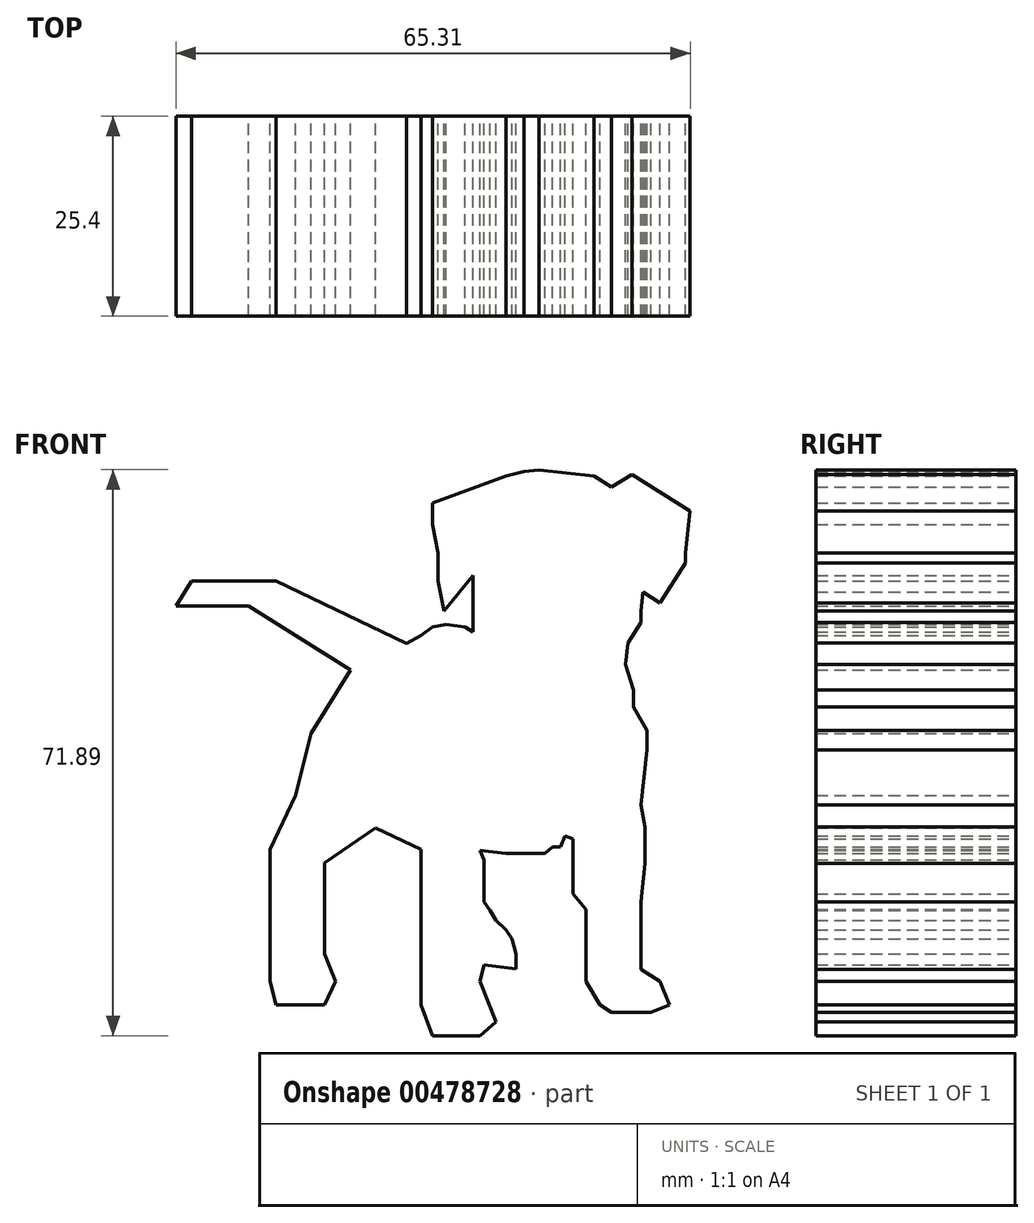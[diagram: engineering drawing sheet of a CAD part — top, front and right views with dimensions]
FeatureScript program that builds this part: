
annotation { "Feature Type Name" : "Feature", "Feature Type Description" : "" }
export const myFeature = defineFeature(function(context is Context, id is Id, definition is map)
    precondition{}
    {
        {
            var Q0;
            Q0=qCreatedBy(makeId("Front.planeOp"),FACE);
            var sketch = newSketch(context, id + "F0", { "sketchPlane" : qUnion([Q0])});
            skLineSegment(sketch, "E0", {"start": v(-38.63, 10.65) * mm, "end": v(-36.66, 13.81) * mm});
            skLineSegment(sketch, "E1", {"start": v(-36.66, 13.81) * mm, "end": v(-25.96, 13.81) * mm});
            skLineSegment(sketch, "E2", {"start": v(-25.96, 13.81) * mm, "end": v(-9.37, 5.92) * mm});
            skLineSegment(sketch, "E3", {"start": v(-38.63, 10.65) * mm, "end": v(-29.44, 10.65) * mm});
            skLineSegment(sketch, "E4", {"start": v(-29.44, 10.65) * mm, "end": v(-16.45, 2.53) * mm});
            skLineSegment(sketch, "E5", {"start": v(-16.45, 2.53) * mm, "end": v(-21.47, -5.5) * mm});
            skLineSegment(sketch, "E6", {"start": v(-21.47, -5.5) * mm, "end": v(-23.45, -13.38) * mm});
            skLineSegment(sketch, "E7", {"start": v(-23.45, -13.38) * mm, "end": v(-26.72, -20.26) * mm});
            skLineSegment(sketch, "E8", {"start": v(-26.72, -20.26) * mm, "end": v(-26.72, -24.45) * mm});
            skLineSegment(sketch, "E9", {"start": v(-26.72, -24.45) * mm, "end": v(-26.72, -37.05) * mm});
            skLineSegment(sketch, "E10", {"start": v(-26.72, -37.05) * mm, "end": v(-25.96, -40) * mm});
            skLineSegment(sketch, "E11", {"start": v(-25.96, -40) * mm, "end": v(-19.76, -40) * mm});
            skLineSegment(sketch, "E12", {"start": v(-19.76, -40) * mm, "end": v(-18.35, -37.05) * mm});
            skLineSegment(sketch, "E13", {"start": v(-18.35, -37.05) * mm, "end": v(-19.76, -33.56) * mm});
            skLineSegment(sketch, "E14", {"start": v(-19.76, -33.56) * mm, "end": v(-19.76, -28.5) * mm});
            skLineSegment(sketch, "E15", {"start": v(-19.76, -28.5) * mm, "end": v(-19.76, -21.96) * mm});
            skLineSegment(sketch, "E16", {"start": v(-19.76, -21.96) * mm, "end": v(-13.27, -17.53) * mm});
            skLineSegment(sketch, "E17", {"start": v(-13.27, -17.53) * mm, "end": v(-7.53, -20.26) * mm});
            skLineSegment(sketch, "E18", {"start": v(-7.53, -20.26) * mm, "end": v(-7.53, -37.05) * mm});
            skLineSegment(sketch, "E19", {"start": v(-7.53, -37.05) * mm, "end": v(-7.53, -40) * mm});
            skLineSegment(sketch, "E20", {"start": v(-7.53, -40) * mm, "end": v(-6.04, -43.92) * mm});
            skLineSegment(sketch, "E21", {"start": v(-6.04, -43.92) * mm, "end": v(0, -43.92) * mm});
            skLineSegment(sketch, "E22", {"start": v(0, -43.92) * mm, "end": v(2.03, -42.19) * mm});
            skLineSegment(sketch, "E23", {"start": v(2.03, -42.19) * mm, "end": v(0, -37.05) * mm});
            skLineSegment(sketch, "E24", {"start": v(0, -37.05) * mm, "end": v(-0.89, -32.5) * mm});
            skLineSegment(sketch, "E25", {"start": v(-0.89, -32.5) * mm, "end": v(-0.89, -30.46) * mm});
            skLineSegment(sketch, "E26", {"start": v(-0.89, -30.46) * mm, "end": v(-0.89, -28.03) * mm});
            skLineSegment(sketch, "E27", {"start": v(-0.89, -28.03) * mm, "end": v(0, -20.4) * mm});
            skLineSegment(sketch, "E28", {"start": v(0, -20.4) * mm, "end": v(3.3, -20.78) * mm});
            skLineSegment(sketch, "E29", {"start": v(3.3, -20.78) * mm, "end": v(5.54, -20.78) * mm});
            skLineSegment(sketch, "E30", {"start": v(5.54, -20.78) * mm, "end": v(7.21, -20.78) * mm});
            skLineSegment(sketch, "E31", {"start": v(7.21, -20.78) * mm, "end": v(8.24, -20.78) * mm});
            skLineSegment(sketch, "E32", {"start": v(8.24, -20.78) * mm, "end": v(9.17, -19.93) * mm});
            skLineSegment(sketch, "E33", {"start": v(9.17, -19.93) * mm, "end": v(10.2, -19.93) * mm});
            skLineSegment(sketch, "E34", {"start": v(10.2, -19.93) * mm, "end": v(10.75, -18.54) * mm});
            skLineSegment(sketch, "E35", {"start": v(10.75, -18.54) * mm, "end": v(11.8, -18.95) * mm});
            skLineSegment(sketch, "E36", {"start": v(11.8, -18.95) * mm, "end": v(11.8, -25.9) * mm});
            skLineSegment(sketch, "E37", {"start": v(11.8, -25.9) * mm, "end": v(13.45, -27.85) * mm});
            skLineSegment(sketch, "E38", {"start": v(13.45, -27.85) * mm, "end": v(13.45, -37.05) * mm});
            skLineSegment(sketch, "E39", {"start": v(13.45, -37.05) * mm, "end": v(15.22, -40) * mm});
            skLineSegment(sketch, "E40", {"start": v(15.22, -40) * mm, "end": v(16.7, -40.93) * mm});
            skLineSegment(sketch, "E41", {"start": v(16.7, -40.93) * mm, "end": v(21.7, -40.93) * mm});
            skLineSegment(sketch, "E42", {"start": v(21.7, -40.93) * mm, "end": v(24.03, -40) * mm});
            skLineSegment(sketch, "E43", {"start": v(24.03, -40) * mm, "end": v(22.87, -37.05) * mm});
            skLineSegment(sketch, "E44", {"start": v(22.87, -37.05) * mm, "end": v(20.4, -35.5) * mm});
            skLineSegment(sketch, "E45", {"start": v(20.4, -35.5) * mm, "end": v(20.4, -32.5) * mm});
            skLineSegment(sketch, "E46", {"start": v(20.4, -32.5) * mm, "end": v(20.4, -26.9) * mm});
            skLineSegment(sketch, "E47", {"start": v(20.4, -26.9) * mm, "end": v(20.96, -22.04) * mm});
            skLineSegment(sketch, "E48", {"start": v(20.96, -22.04) * mm, "end": v(20.96, -17.42) * mm});
            skLineSegment(sketch, "E49", {"start": v(20.96, -17.42) * mm, "end": v(20.4, -14.63) * mm});
            skLineSegment(sketch, "E50", {"start": v(20.4, -14.63) * mm, "end": v(20.84, -10.8) * mm});
            skLineSegment(sketch, "E51", {"start": v(20.84, -10.8) * mm, "end": v(21.2, -7.65) * mm});
            skLineSegment(sketch, "E52", {"start": v(21.2, -7.65) * mm, "end": v(21.2, -5.15) * mm});
            skLineSegment(sketch, "E53", {"start": v(21.2, -5.15) * mm, "end": v(19.46, -2.14) * mm});
            skLineSegment(sketch, "E54", {"start": v(19.46, -2.14) * mm, "end": v(19.46, 0) * mm});
            skLineSegment(sketch, "E55", {"start": v(19.46, 0) * mm, "end": v(18.46, 3.21) * mm});
            skLineSegment(sketch, "E56", {"start": v(18.46, 3.21) * mm, "end": v(18.78, 5.97) * mm});
            skLineSegment(sketch, "E57", {"start": v(18.78, 5.97) * mm, "end": v(20.4, 8.56) * mm});
            skLineSegment(sketch, "E58", {"start": v(20.4, 8.56) * mm, "end": v(20.4, 10.02) * mm});
            skLineSegment(sketch, "E59", {"start": v(20.4, 10.02) * mm, "end": v(20.68, 12.42) * mm});
            skLineSegment(sketch, "E60", {"start": v(20.68, 12.42) * mm, "end": v(22.87, 11.06) * mm});
            skLineSegment(sketch, "E61", {"start": v(22.87, 11.06) * mm, "end": v(23.72, 12.42) * mm});
            skLineSegment(sketch, "E62", {"start": v(23.72, 12.42) * mm, "end": v(26.05, 16.16) * mm});
            skLineSegment(sketch, "E63", {"start": v(26.05, 16.16) * mm, "end": v(26.05, 17.38) * mm});
            skLineSegment(sketch, "E64", {"start": v(26.05, 17.38) * mm, "end": v(26.48, 21) * mm});
            skLineSegment(sketch, "E65", {"start": v(26.48, 21) * mm, "end": v(26.68, 22.74) * mm});
            skLineSegment(sketch, "E66", {"start": v(26.68, 22.74) * mm, "end": v(19.28, 27.36) * mm});
            skLineSegment(sketch, "E67", {"start": v(19.28, 27.36) * mm, "end": v(16.7, 25.76) * mm});
            skLineSegment(sketch, "E68", {"start": v(16.7, 25.76) * mm, "end": v(14.49, 27.15) * mm});
            skLineSegment(sketch, "E69", {"start": v(14.49, 27.15) * mm, "end": v(12.62, 27.37) * mm});
            skLineSegment(sketch, "E70", {"start": v(12.62, 27.37) * mm, "end": v(10.88, 27.57) * mm});
            skLineSegment(sketch, "E71", {"start": v(10.88, 27.57) * mm, "end": v(9.17, 27.77) * mm});
            skLineSegment(sketch, "E72", {"start": v(9.17, 27.77) * mm, "end": v(7.45, 27.97) * mm});
            skLineSegment(sketch, "E73", {"start": v(7.45, 27.97) * mm, "end": v(5.54, 27.77) * mm});
            skLineSegment(sketch, "E74", {"start": v(5.54, 27.77) * mm, "end": v(3.3, 27.15) * mm});
            skLineSegment(sketch, "E75", {"start": v(3.3, 27.15) * mm, "end": v(-6.04, 23.72) * mm});
            skLineSegment(sketch, "E76", {"start": v(-6.04, 23.72) * mm, "end": v(-6.04, 21) * mm});
            skLineSegment(sketch, "E77", {"start": v(-6.04, 21) * mm, "end": v(-5.35, 17.38) * mm});
            skLineSegment(sketch, "E78", {"start": v(-5.35, 17.38) * mm, "end": v(-5.35, 13.87) * mm});
            skLineSegment(sketch, "E79", {"start": v(-5.35, 13.87) * mm, "end": v(-4.62, 10.02) * mm});
            skLineSegment(sketch, "E80", {"start": v(-4.62, 10.02) * mm, "end": v(-0.89, 14.52) * mm});
            skLineSegment(sketch, "E81", {"start": v(-0.89, 14.52) * mm, "end": v(-0.89, 7.37) * mm});
            skLineSegment(sketch, "E82", {"start": v(-0.89, 7.37) * mm, "end": v(-1.92, 8.02) * mm});
            skLineSegment(sketch, "E83", {"start": v(-1.92, 8.02) * mm, "end": v(-3.07, 8.15) * mm});
            skLineSegment(sketch, "E84", {"start": v(-3.07, 8.15) * mm, "end": v(-4.34, 8.3) * mm});
            skLineSegment(sketch, "E85", {"start": v(-4.34, 8.3) * mm, "end": v(-6.04, 8.02) * mm});
            skLineSegment(sketch, "E86", {"start": v(-6.04, 8.02) * mm, "end": v(-7.53, 6.93) * mm});
            skLineSegment(sketch, "E87", {"start": v(-7.53, 6.93) * mm, "end": v(-9.37, 5.92) * mm});
            skLineSegment(sketch, "E88", {"start": v(0.52, -21.58) * mm, "end": v(0.52, -23.52) * mm});
            skLineSegment(sketch, "E89", {"start": v(0.52, -23.52) * mm, "end": v(0.52, -24.88) * mm});
            skLineSegment(sketch, "E90", {"start": v(0.52, -24.88) * mm, "end": v(0.52, -26.9) * mm});
            skLineSegment(sketch, "E91", {"start": v(0.52, -26.9) * mm, "end": v(1.23, -28.03) * mm});
            skLineSegment(sketch, "E92", {"start": v(1.23, -28.03) * mm, "end": v(2.03, -29.25) * mm});
            skLineSegment(sketch, "E93", {"start": v(2.03, -29.25) * mm, "end": v(3.3, -30.46) * mm});
            skLineSegment(sketch, "E94", {"start": v(3.3, -30.46) * mm, "end": v(4.03, -31.61) * mm});
            skLineSegment(sketch, "E95", {"start": v(4.03, -31.61) * mm, "end": v(4.53, -33.56) * mm});
            skLineSegment(sketch, "E96", {"start": v(4.53, -33.56) * mm, "end": v(4.53, -34.48) * mm});
            skLineSegment(sketch, "E97", {"start": v(4.53, -34.48) * mm, "end": v(4.53, -35.4) * mm});
            skLineSegment(sketch, "E98", {"start": v(4.53, -35.4) * mm, "end": v(3.3, -35.26) * mm});
            skLineSegment(sketch, "E99", {"start": v(3.3, -35.26) * mm, "end": v(2.03, -35.12) * mm});
            skLineSegment(sketch, "E100", {"start": v(2.03, -35.12) * mm, "end": v(0.52, -34.94) * mm});
            skLineSegment(sketch, "E101", {"start": v(0.52, -34.94) * mm, "end": v(0, -37.05) * mm});
            skLineSegment(sketch, "E102", {"start": v(0.52, -21.58) * mm, "end": v(0, -20.4) * mm});
            skSolve(sketch);
        }
        {
            var Q0;
            Q0=makeQuery(id+"F0.imprint","IMPRINT",FACE,{"disambiguationData":[TD([[makeQuery(id+"F0.imprint","IMPRINT",EDGE,{"derivedFrom":sQuery(id+"F0.wireOp",EDGE,"E0")}),-1.0]])]});
            var Q1;
            Q1=makeQuery(id+"F0.imprint","IMPRINT",FACE,{"disambiguationData":[TD([[makeQuery(id+"F0.imprint","IMPRINT",EDGE,{"derivedFrom":sQuery(id+"F0.wireOp",EDGE,"E24")}),-1.0]])]});
            extrude(context, id + "F1", {"entities" : qUnion([Q0, Q1]), "depth" : 25.4 * mm});
        }
    });
